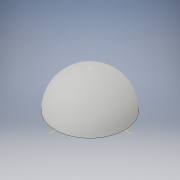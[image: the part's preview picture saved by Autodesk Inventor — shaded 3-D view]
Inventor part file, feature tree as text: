
AUTODESK INVENTOR PART (.ipt)
format: ipt  version: 2018 (Build 220112000, 112)  size: 123,392 bytes
history: native  units: in
note: dims shown in document units (in); Inventor stores cm internally (conversion verified against a paired STEP export)
features: revolve x1, sketch x1
ambient origin geometry x8: Origin, YZ Plane, XZ Plane, XY Plane, X Axis, Y Axis, Z Axis, Center Point
bodies: Solid1 (feature_tree)
feature tree (2):
  revolve  "Revolution1"  Angle=180.0deg
  sketch  "Sketch2"  dims[d0=78.1496in d1=180.0deg]
